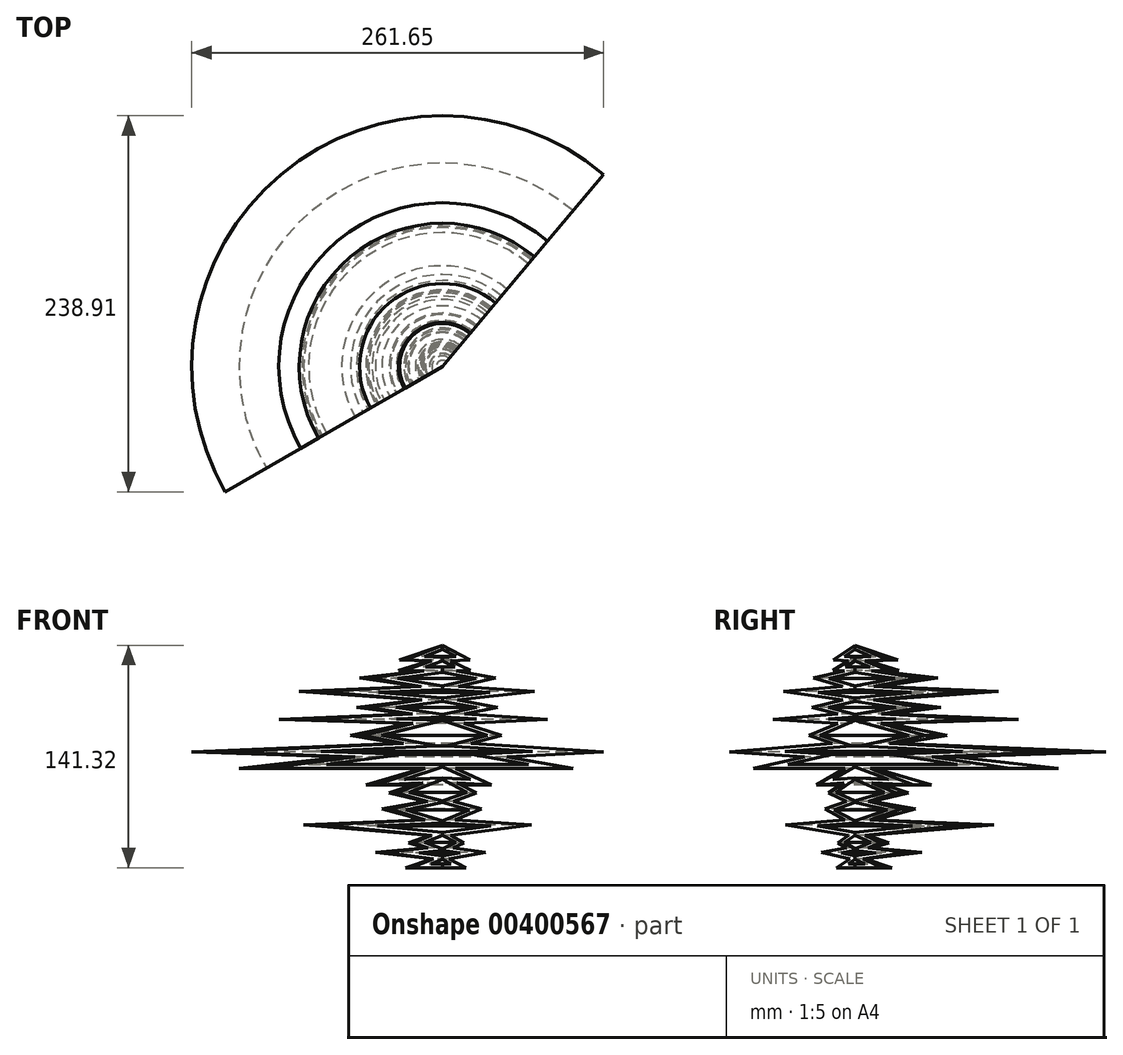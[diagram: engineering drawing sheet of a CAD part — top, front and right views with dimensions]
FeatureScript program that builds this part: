
annotation { "Feature Type Name" : "Feature", "Feature Type Description" : "" }
export const myFeature = defineFeature(function(context is Context, id is Id, definition is map)
    precondition{}
    {
        {
            var Q0;
            Q0=qCreatedBy(makeId("Front.planeOp"),FACE);
            var sketch = newSketch(context, id + "F0", { "sketchPlane" : qUnion([Q0])});
            skLineSegment(sketch, "E0", {"start": v(48.67, 70.78) * mm, "end": v(48.67, -70.54) * mm});
            skLineSegment(sketch, "E1", {"start": v(48.67, -70.54) * mm, "end": v(25.33, -70.54) * mm});
            skLineSegment(sketch, "E2", {"start": v(25.33, -70.54) * mm, "end": v(42, -64.73) * mm});
            skLineSegment(sketch, "E3", {"start": v(42, -64.73) * mm, "end": v(6.14, -60.82) * mm});
            skLineSegment(sketch, "E4", {"start": v(6.14, -60.82) * mm, "end": v(38.04, -57.86) * mm});
            skLineSegment(sketch, "E5", {"start": v(38.04, -57.86) * mm, "end": v(27.2, -54.57) * mm});
            skLineSegment(sketch, "E6", {"start": v(27.2, -54.57) * mm, "end": v(40.52, -50) * mm});
            skLineSegment(sketch, "E7", {"start": v(40.52, -50) * mm, "end": v(-39.44, -43.15) * mm});
            skLineSegment(sketch, "E8", {"start": v(-39.44, -43.15) * mm, "end": v(36.08, -40.09) * mm});
            skLineSegment(sketch, "E9", {"start": v(36.08, -40.09) * mm, "end": v(10.19, -33.1) * mm});
            skLineSegment(sketch, "E10", {"start": v(10.19, -33.1) * mm, "end": v(37.65, -28.22) * mm});
            skLineSegment(sketch, "E11", {"start": v(37.65, -28.22) * mm, "end": v(14.83, -22.93) * mm});
            skLineSegment(sketch, "E12", {"start": v(14.83, -22.93) * mm, "end": v(34.51, -16.46) * mm});
            skLineSegment(sketch, "E13", {"start": v(34.51, -16.46) * mm, "end": v(0, -17.86) * mm});
            skLineSegment(sketch, "E14", {"start": v(0, -17.86) * mm, "end": v(35.89, -7.52) * mm});
            skLineSegment(sketch, "E15", {"start": v(35.89, -7.52) * mm, "end": v(-80.44, -7.52) * mm});
            skLineSegment(sketch, "E16", {"start": v(-80.44, -7.52) * mm, "end": v(-15.28, 0) * mm});
            skLineSegment(sketch, "E17", {"start": v(-15.28, 0) * mm, "end": v(-110.6, 3.04) * mm});
            skLineSegment(sketch, "E18", {"start": v(-110.6, 3.04) * mm, "end": v(20.27, 8.35) * mm});
            skLineSegment(sketch, "E19", {"start": v(20.27, 8.35) * mm, "end": v(-9.74, 13.4) * mm});
            skLineSegment(sketch, "E20", {"start": v(-9.74, 13.4) * mm, "end": v(27.27, 21.12) * mm});
            skLineSegment(sketch, "E21", {"start": v(27.27, 21.12) * mm, "end": v(-55.26, 23.76) * mm});
            skLineSegment(sketch, "E22", {"start": v(-55.26, 23.76) * mm, "end": v(26.74, 27.08) * mm});
            skLineSegment(sketch, "E23", {"start": v(26.74, 27.08) * mm, "end": v(-5.88, 31.4) * mm});
            skLineSegment(sketch, "E24", {"start": v(-5.88, 31.4) * mm, "end": v(33.58, 35.95) * mm});
            skLineSegment(sketch, "E25", {"start": v(33.58, 35.95) * mm, "end": v(-42.27, 41.61) * mm});
            skLineSegment(sketch, "E26", {"start": v(-42.27, 41.61) * mm, "end": v(32.92, 44.66) * mm});
            skLineSegment(sketch, "E27", {"start": v(32.92, 44.66) * mm, "end": v(-3.97, 50) * mm});
            skLineSegment(sketch, "E28", {"start": v(-3.97, 50) * mm, "end": v(35, 54.5) * mm});
            skLineSegment(sketch, "E29", {"start": v(35, 54.5) * mm, "end": v(20.8, 54.95) * mm});
            skLineSegment(sketch, "E30", {"start": v(20.8, 54.95) * mm, "end": v(40.52, 60.9) * mm});
            skLineSegment(sketch, "E31", {"start": v(40.52, 60.9) * mm, "end": v(21.49, 61.51) * mm});
            skLineSegment(sketch, "E32", {"start": v(21.49, 61.51) * mm, "end": v(48.67, 70.78) * mm});
            skSolve(sketch);
        }
        {
            var Q0;
            Q0=makeQuery(id+"F0.imprint","IMPRINT",FACE,{"disambiguationData":[TD([[makeQuery(id+"F0.imprint","IMPRINT",EDGE,{"derivedFrom":sQuery(id+"F0.wireOp",EDGE,"E0")}),-1.0]])]});
            var Q1;
            Q1=sQuery(id+"F0.wireOp",EDGE,"E0");
            revolve(context, id + "F1", {"entities" : qUnion([Q0]), "axis" : qUnion([Q1]), "revolveType" : RevolveType.TWO_DIRECTIONS, "angle" : 130 * degree, "angleBack" : 330 * degree});
        }
        {
            var Q0;
            Q0=makeQuery(id+"F1.opRevolve","CAP_FACE",FACE,{"disambiguationData":[OSD([sQuery(id+"F0.wireOp",EDGE,"E0"),sQuery(id+"F0.wireOp",EDGE,"E1"),sQuery(id+"F0.wireOp",EDGE,"E2"),sQuery(id+"F0.wireOp",EDGE,"E3"),sQuery(id+"F0.wireOp",EDGE,"E4"),sQuery(id+"F0.wireOp",EDGE,"E5"),sQuery(id+"F0.wireOp",EDGE,"E6"),sQuery(id+"F0.wireOp",EDGE,"E7"),sQuery(id+"F0.wireOp",EDGE,"E8"),sQuery(id+"F0.wireOp",EDGE,"E9"),sQuery(id+"F0.wireOp",EDGE,"E10"),sQuery(id+"F0.wireOp",EDGE,"E11"),sQuery(id+"F0.wireOp",EDGE,"E12"),sQuery(id+"F0.wireOp",EDGE,"E13"),sQuery(id+"F0.wireOp",EDGE,"E14"),sQuery(id+"F0.wireOp",EDGE,"E15"),sQuery(id+"F0.wireOp",EDGE,"E16"),sQuery(id+"F0.wireOp",EDGE,"E17"),sQuery(id+"F0.wireOp",EDGE,"E18"),sQuery(id+"F0.wireOp",EDGE,"E19"),sQuery(id+"F0.wireOp",EDGE,"E20"),sQuery(id+"F0.wireOp",EDGE,"E21"),sQuery(id+"F0.wireOp",EDGE,"E22"),sQuery(id+"F0.wireOp",EDGE,"E23"),sQuery(id+"F0.wireOp",EDGE,"E24"),sQuery(id+"F0.wireOp",EDGE,"E25"),sQuery(id+"F0.wireOp",EDGE,"E26"),sQuery(id+"F0.wireOp",EDGE,"E27"),sQuery(id+"F0.wireOp",EDGE,"E28"),sQuery(id+"F0.wireOp",EDGE,"E29"),sQuery(id+"F0.wireOp",EDGE,"E30"),sQuery(id+"F0.wireOp",EDGE,"E31"),sQuery(id+"F0.wireOp",EDGE,"E32")])],"isStart":false});
            var Q1;
            Q1=makeQuery(id+"F1.opRevolve","CAP_FACE",FACE,{"disambiguationData":[OSD([sQuery(id+"F0.wireOp",EDGE,"E0"),sQuery(id+"F0.wireOp",EDGE,"E1"),sQuery(id+"F0.wireOp",EDGE,"E2"),sQuery(id+"F0.wireOp",EDGE,"E3"),sQuery(id+"F0.wireOp",EDGE,"E4"),sQuery(id+"F0.wireOp",EDGE,"E5"),sQuery(id+"F0.wireOp",EDGE,"E6"),sQuery(id+"F0.wireOp",EDGE,"E7"),sQuery(id+"F0.wireOp",EDGE,"E8"),sQuery(id+"F0.wireOp",EDGE,"E9"),sQuery(id+"F0.wireOp",EDGE,"E10"),sQuery(id+"F0.wireOp",EDGE,"E11"),sQuery(id+"F0.wireOp",EDGE,"E12"),sQuery(id+"F0.wireOp",EDGE,"E13"),sQuery(id+"F0.wireOp",EDGE,"E14"),sQuery(id+"F0.wireOp",EDGE,"E15"),sQuery(id+"F0.wireOp",EDGE,"E16"),sQuery(id+"F0.wireOp",EDGE,"E17"),sQuery(id+"F0.wireOp",EDGE,"E18"),sQuery(id+"F0.wireOp",EDGE,"E19"),sQuery(id+"F0.wireOp",EDGE,"E20"),sQuery(id+"F0.wireOp",EDGE,"E21"),sQuery(id+"F0.wireOp",EDGE,"E22"),sQuery(id+"F0.wireOp",EDGE,"E23"),sQuery(id+"F0.wireOp",EDGE,"E24"),sQuery(id+"F0.wireOp",EDGE,"E25"),sQuery(id+"F0.wireOp",EDGE,"E26"),sQuery(id+"F0.wireOp",EDGE,"E27"),sQuery(id+"F0.wireOp",EDGE,"E28"),sQuery(id+"F0.wireOp",EDGE,"E29"),sQuery(id+"F0.wireOp",EDGE,"E30"),sQuery(id+"F0.wireOp",EDGE,"E31"),sQuery(id+"F0.wireOp",EDGE,"E32")])],"isStart":true});
            shell(context, id + "F2", {"entities" : qUnion([Q0, Q1]), "thickness" : 2.54 * mm});
        }
    });
